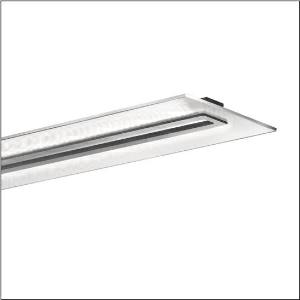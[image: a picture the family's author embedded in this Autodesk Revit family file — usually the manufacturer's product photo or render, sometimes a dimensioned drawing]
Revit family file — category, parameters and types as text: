
# Revit family: vega_r__11_5mn238dlc003_c003
name_source: partatom
category: Lighting Fixtures
units: mm (PartAtom-declared; Revit-internal decimal feet)

## family parameters
Cut with Voids When Loaded = No
Host = Face
Light Source = No
Part Type = Normal
Room Calculation Point = No
Round Connector Dimension = Use Diameter
Shared = No

## types (1)
- --- (1 x LED 3000K / CRI = 80 (unbekannt), 4300 lm, 3000K)
    Apparent Load = 35 VA
    CIE Flux Codes = 61 86 97 62 100
    Color Rendering = 80
    Color Temperature = 3000K
    Default Elevation = 1800 mm
    Description = Vega® 11, office luminaire, primary light control with prismatic reflector, of PMMA, transparent prismatic structure, CAT 2 (L<= 1500cd/m²), light emission: direct/indirect distribution, primary light characteristic: symmetric, installation type: suspended mounting, surface-mounted, LED, rated luminous flux: 4.300lm, luminous efficacy: 123lm/W, light colour: 830, colour temperature: 3000K, control gear: ECG, with terminal, 3+2-pole, max. 2.5mm², mains connection: 230V, AC, 50Hz, connection cable inclusive, cable length: 1,5m, rated input power: 35W, luminaire housing, rectangular, rounded, of aluminium section, anodised, metallic grey (RAL 9006), length: 1.250mm, width: 350mm, height: 43mm, luminaire housing, lower part, of aluminium section, anodised, metallic grey (RAL 9006), of PC, grey, protection rating (complete): IP20, insulation class (complete): insulation class I (protective earthing), certification: CE, standard: EN 50419, packaging unit: 1 piece
    Height = 40 mm  [stored 0.131234 ft]
    Lamp = 1 x LED 3000K / CRI >= 80 (unbekannt)
    Lamp Light Flux = 4300 lm
    Lamp count = 1
    Length = 1250 mm
    Luminous efficacy = 123 lm/W
    Manufacturer = Siteco
    ModVariant = No
    Model = 5MN238DLC003
    Mounting Place = Ceiling
    Mounting Type = Pendant
    Number of Poles = 1
    OnlyDefault = Yes
    Power Factor = 1
    Product Name = Vega® 11
    Product group = office luminaire | ceiling pendant
    ProductGroupID = 902
    Protection Class = Protection class I
    Protection Degree = IP 20
    RLX_Detail_Level = 1
    RLX_Emergency_Light_Flux = 0 lm
    RLX_Emergency_Type = 0
    RLX_Emergency_Type_DB = No
    RlxData = <blob elided: 62813 chars, md5=59295f1d>
    Socket = socket
    Standby Power = 0 W
    System Light Flux = 4300 lm
    System Power = 35 W
    Type Comments = factory setting: luminous flux: 100 % | dim-lin: 254 | 260 mA
    Type Image = l_1004807.jpg
    URL = http://relux.com
    VarID = @adj_165541
    Voltage = 0 V
    Weight = 0.00 kg
    Width = 350 mm

note: [stored X ft] marks values corroborated as IEEE doubles in the binary element streams (Revit-internal decimal feet)

## geometry (parser evidence)
native form markers: Blend x4, Sweep x13
no freeform markers — native parametric forms only
